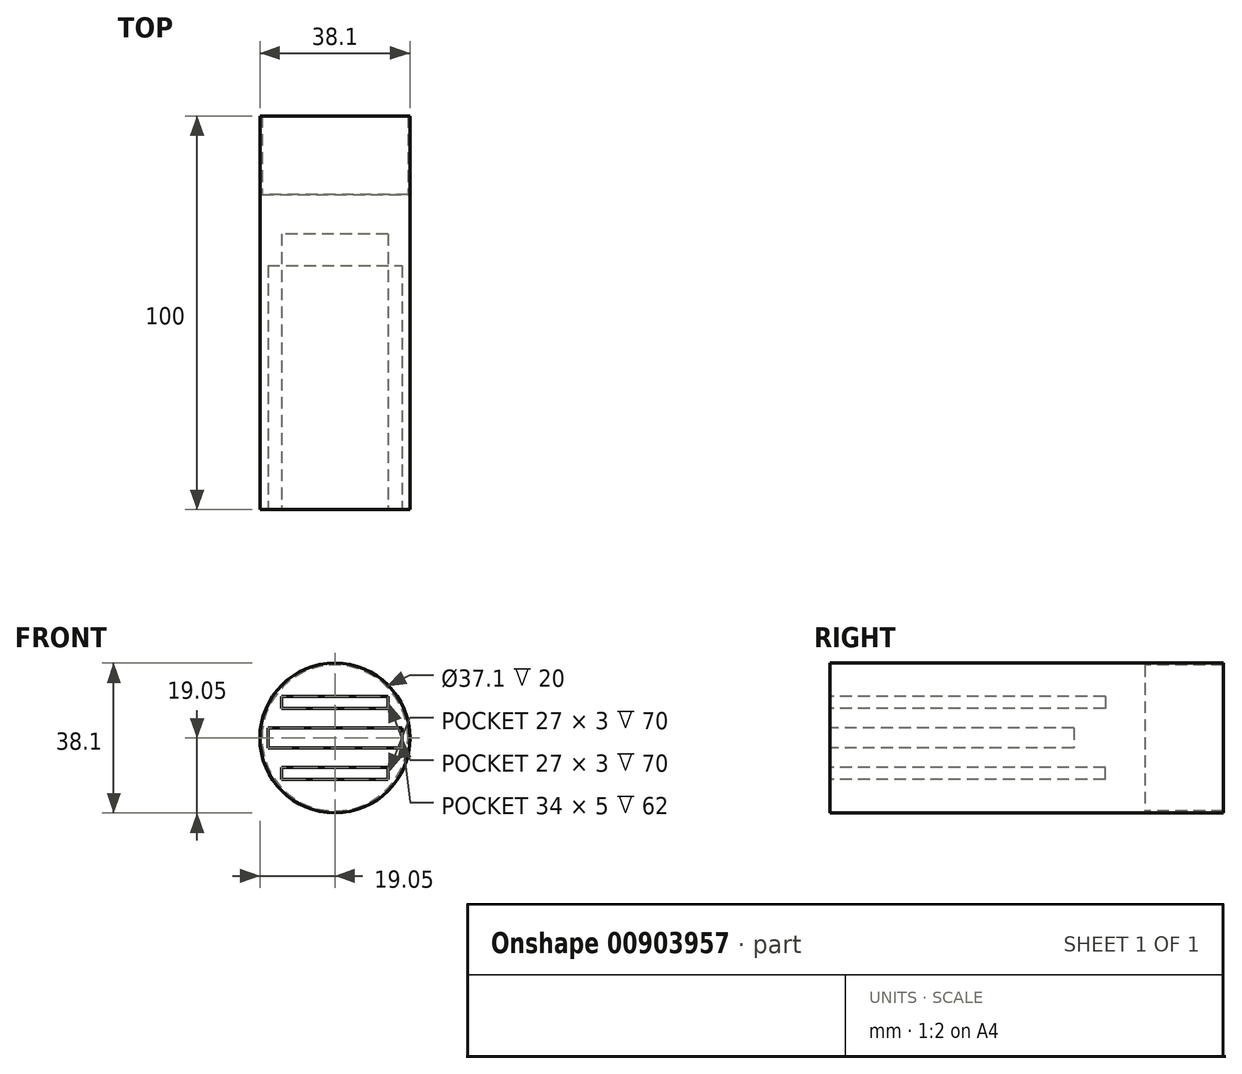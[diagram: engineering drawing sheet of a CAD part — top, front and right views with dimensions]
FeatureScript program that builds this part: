
annotation { "Feature Type Name" : "Feature", "Feature Type Description" : "" }
export const myFeature = defineFeature(function(context is Context, id is Id, definition is map)
    precondition{}
    {
        {
            var Q0;
            Q0=qCreatedBy(makeId("Front.planeOp"),FACE);
            var sketch = newSketch(context, id + "F0", { "sketchPlane" : qUnion([Q0])});
            skCircle(sketch, "E0", {"center": v(0, 0) * mm, "radius": 19.05 * mm});
            skSolve(sketch);
        }
        {
            var Q0;
            Q0=makeQuery(id+"F0.imprint","IMPRINT",FACE,{"disambiguationData":[TD([[makeQuery(id+"F0.imprint","IMPRINT",EDGE,{"derivedFrom":sQuery(id+"F0.wireOp",EDGE,"E0")}),1.0]])]});
            extrude(context, id + "F1", {"entities" : qUnion([Q0]), "oppositeDirection" : true, "depth" : 80 * mm, "offsetDistance" : 25.4 * mm});
        }
        {
            var Q0;
            Q0=makeQuery(id+"F1.opExtrude","CAP_FACE",FACE,{"disambiguationData":[OSD([sQuery(id+"F0.wireOp",EDGE,"E0")])],"isStart":true});
            var sketch = newSketch(context, id + "F2", { "sketchPlane" : qUnion([Q0])});
            skCircle(sketch, "E1", {"center": v(-10, 0) * mm, "radius": 7 * mm});
            skLineSegment(sketch, "E2", {"start": v(-10, 0) * mm, "end": v(0, 0) * mm, "construction": true});
            skCircle(sketch, "E3.MirrorC", {"center": v(10, 0) * mm, "radius": 7 * mm});
            skLineSegment(sketch, "E4.MirrorCS", {"start": v(10, 0) * mm, "end": v(0, 0) * mm, "construction": true});
            skSolve(sketch);
        }
        {
            var Q0;
            Q0=qCreatedBy(makeId("Front.planeOp"),FACE);
            var sketch = newSketch(context, id + "F3", { "sketchPlane" : qUnion([Q0])});
            skLineSegment(sketch, "E5.bottom", {"start": v(-13.5, 10.5) * mm, "end": v(13.5, 10.5) * mm});
            skLineSegment(sketch, "E5.top", {"start": v(-13.5, 7.5) * mm, "end": v(13.5, 7.5) * mm});
            skLineSegment(sketch, "E5.left", {"start": v(-13.5, 10.5) * mm, "end": v(-13.5, 7.5) * mm});
            skLineSegment(sketch, "E5.right", {"start": v(13.5, 10.5) * mm, "end": v(13.5, 7.5) * mm});
            skLineSegment(sketch, "E6", {"start": v(0, 0) * mm, "end": v(0, 18.98) * mm, "construction": true});
            skLineSegment(sketch, "E7.MirrorCS", {"start": v(13.5, 7.5) * mm, "end": v(-13.5, 7.5) * mm});
            skLineSegment(sketch, "E8.MirrorCS", {"start": v(13.5, 10.5) * mm, "end": v(-13.5, 10.5) * mm});
            skLineSegment(sketch, "E9", {"start": v(0, 0) * mm, "end": v(49.77, 0) * mm, "construction": true});
            skLineSegment(sketch, "E10.MirrorCS", {"start": v(13.5, -10.5) * mm, "end": v(13.5, -7.5) * mm});
            skLineSegment(sketch, "E11.MirrorCS", {"start": v(-13.5, -10.5) * mm, "end": v(-13.5, -7.5) * mm});
            skLineSegment(sketch, "E12.MirrorCS", {"start": v(13.5, -7.5) * mm, "end": v(-13.5, -7.5) * mm});
            skLineSegment(sketch, "E13.MirrorCS", {"start": v(-13.5, -10.5) * mm, "end": v(13.5, -10.5) * mm});
            skLineSegment(sketch, "E14.MirrorCS", {"start": v(-13.5, -7.5) * mm, "end": v(13.5, -7.5) * mm});
            skLineSegment(sketch, "E15.MirrorCS", {"start": v(13.5, -10.5) * mm, "end": v(-13.5, -10.5) * mm});
            skCircle(sketch, "E16.0", {"center": v(0, 0) * mm, "radius": 17.85 * mm});
            skSolve(sketch);
        }
        {
            var Q0;
            Q0=makeQuery(id+"F1.opExtrude","CAP_FACE",FACE,{"disambiguationData":[OSD([sQuery(id+"F0.wireOp",EDGE,"E0"),sQuery(id+"F0.wireOp",EDGE,"NDq5s5N3-NFOX-lJ1c-E1gb-axoDSuyLAQJT")])],"isStart":false});
            var sketch = newSketch(context, id + "F4", { "sketchPlane" : qUnion([Q0])});
            skCircle(sketch, "E17", {"center": v(0, 0) * mm, "radius": 19.05 * mm});
            skCircle(sketch, "E18", {"center": v(0, 0) * mm, "radius": 18.55 * mm});
            skSolve(sketch);
        }
        {
            var Q0;
            Q0=makeQuery(id+"F4.imprint","IMPRINT",FACE,{"disambiguationData":[TD([[makeQuery(id+"F4.imprint","IMPRINT",EDGE,{"derivedFrom":sQuery(id+"F4.wireOp",EDGE,"E17")}),-1.0]])]});
            extrude(context, id + "F5", {"entities" : qUnion([Q0]), "operationType" : NewBodyOperationType.ADD, "depth" : 20 * mm, "offsetDistance" : 25 * mm});
        }
        {
            var Q0;
            Q0=makeQuery(id+"F3.imprint","IMPRINT",FACE,{"disambiguationData":[TD([[makeQuery(id+"F3.imprint","IMPRINT",EDGE,{"derivedFrom":sQuery(id+"F3.wireOp",EDGE,"E5.right")}),-1.0]])]});
            var Q1;
            Q1=makeQuery(id+"F3.imprint","IMPRINT",FACE,{"disambiguationData":[TD([[makeQuery(id+"F3.imprint","IMPRINT",EDGE,{"derivedFrom":sQuery(id+"F3.wireOp",EDGE,"E10.MirrorCS")}),1.0]])]});
            extrude(context, id + "F6", {"entities" : qUnion([Q0, Q1]), "operationType" : NewBodyOperationType.REMOVE, "oppositeDirection" : true, "depth" : 70 * mm, "offsetDistance" : 25 * mm});
        }
        {
            var Q0;
            Q0=makeQuery(id+"F6.boolean.opBoolean","COPY",FACE,{"derivedFrom":makeQuery(id+"F6.opExtrude","SWEPT_FACE",FACE,{"disambiguationData":[OSD([sQuery(id+"F3.wireOp",EDGE,"E5.right")])]})});
            cPlane(context, id + "F7", {"entities" : qUnion([Q0]), "cplaneType" : CPlaneType.OFFSET, "offset" : 50 * mm, "width" : 150 * mm, "height" : 150 * mm});
        }
        {
            var Q0;
            Q0=qCreatedBy(makeId("Front.planeOp"),FACE);
            var sketch = newSketch(context, id + "F8", { "sketchPlane" : qUnion([Q0])});
            skLineSegment(sketch, "E19.bottom", {"start": v(-17, 2.5) * mm, "end": v(17, 2.5) * mm});
            skLineSegment(sketch, "E19.top", {"start": v(-17, -2.5) * mm, "end": v(17, -2.5) * mm});
            skLineSegment(sketch, "E19.left", {"start": v(-17, 2.5) * mm, "end": v(-17, -2.5) * mm});
            skLineSegment(sketch, "E19.right", {"start": v(17, 2.5) * mm, "end": v(17, -2.5) * mm});
            skPoint(sketch, "E19.middle", {"position": v(0, 0) * mm});
            skSolve(sketch);
        }
        {
            var Q0;
            Q0=makeQuery(id+"F8.imprint","IMPRINT",FACE,{"disambiguationData":[TD([[makeQuery(id+"F8.imprint","IMPRINT",EDGE,{"derivedFrom":sQuery(id+"F8.wireOp",EDGE,"E19.bottom")}),-1.0]])]});
            extrude(context, id + "F9", {"entities" : qUnion([Q0]), "operationType" : NewBodyOperationType.REMOVE, "oppositeDirection" : true, "depth" : 62 * mm, "offsetDistance" : 25 * mm});
        }
    });
